# Revit family: Hekatron_Feststellanlagen_FSZ Pro_DE_22.01
name_source: partatom
category: Brandmelder
revit_build: Autodesk Revit 2018 (Build: 20190510_1515(x64)
units: mm (PartAtom-declared; Revit-internal decimal feet)

## family parameters
Basisbauteil = Fläche
Beim Laden mit Abzugskörper schneiden = Nein
Bemaßung runder Anschluss = Durchmesser verwenden
Beschriftungsausrichtung beibehalten = Ja
Gemeinsam genutzt = Nein
OmniClass-Nummer = 23.85.30.21
OmniClass-Titel = Environmental Detection/Registration
Raumberechnungspunkt = Nein
Teiletyp = Normal

## types (1)
- FSZ Pro
    Bauartgenehmigungen = Z-6.500-2359
    Beschreibung = Feststellanlagen-Zentrale zum Einsatz in Feststell anlagen an Brand- und Rauchschutztoren und anderen Abschlüssen. VdS geprüft nach den allgemeinen Anforderungen und Prüfgrundlagen für das Zulassungsverfahren für Feststellanlagen und DIBt zugelassen. VdS geprüft und zertifiziert gemäß DIN EN 14637. Bestehend aus Energieversorgung, Auslösevorrichtung, Handtaster, Resettaster und Alarmspeicher.
    Betriebsspannung = 230 V AC
    Breite (mm) = 60.5
    Farbe = weiß, ähnlich RAL 9003
    Hersteller = Hekatron
    Höhe (mm) = 146.0
    Kabeleinführung = oben, unten, hinten
    Lautstärke DIN-Ton (dB) = 65.0
    Link zu Ausschreibungstext = https://www.meinhplus.de
    Link zu ausschreiben.de = http://www.ausschreiben.de
    Material = PC-ABS
    Modell = FSZ Pro
    Montageart = Aufputz
    Nettogewicht (g) = 447.0
    Schutzart = IP 65
    Tiefe (mm) = 146.0
    Typenkommentare = Fest-Stellanlagen-Zentrale Pro
    UB A&S Artikel Nummer = 31-5400003-01-01
    URL = https://www.hekatron-brandschutz.de
    Version des BIM Objektes = 22.01
    Vorgabe-Ansicht = 1200 mm
    Zulässige Umgebungstemperatur = -10 °C bis +45 °C

## geometry (parser evidence)
native form markers: Extrusion x1, Sweep x2
no freeform markers — native parametric forms only
